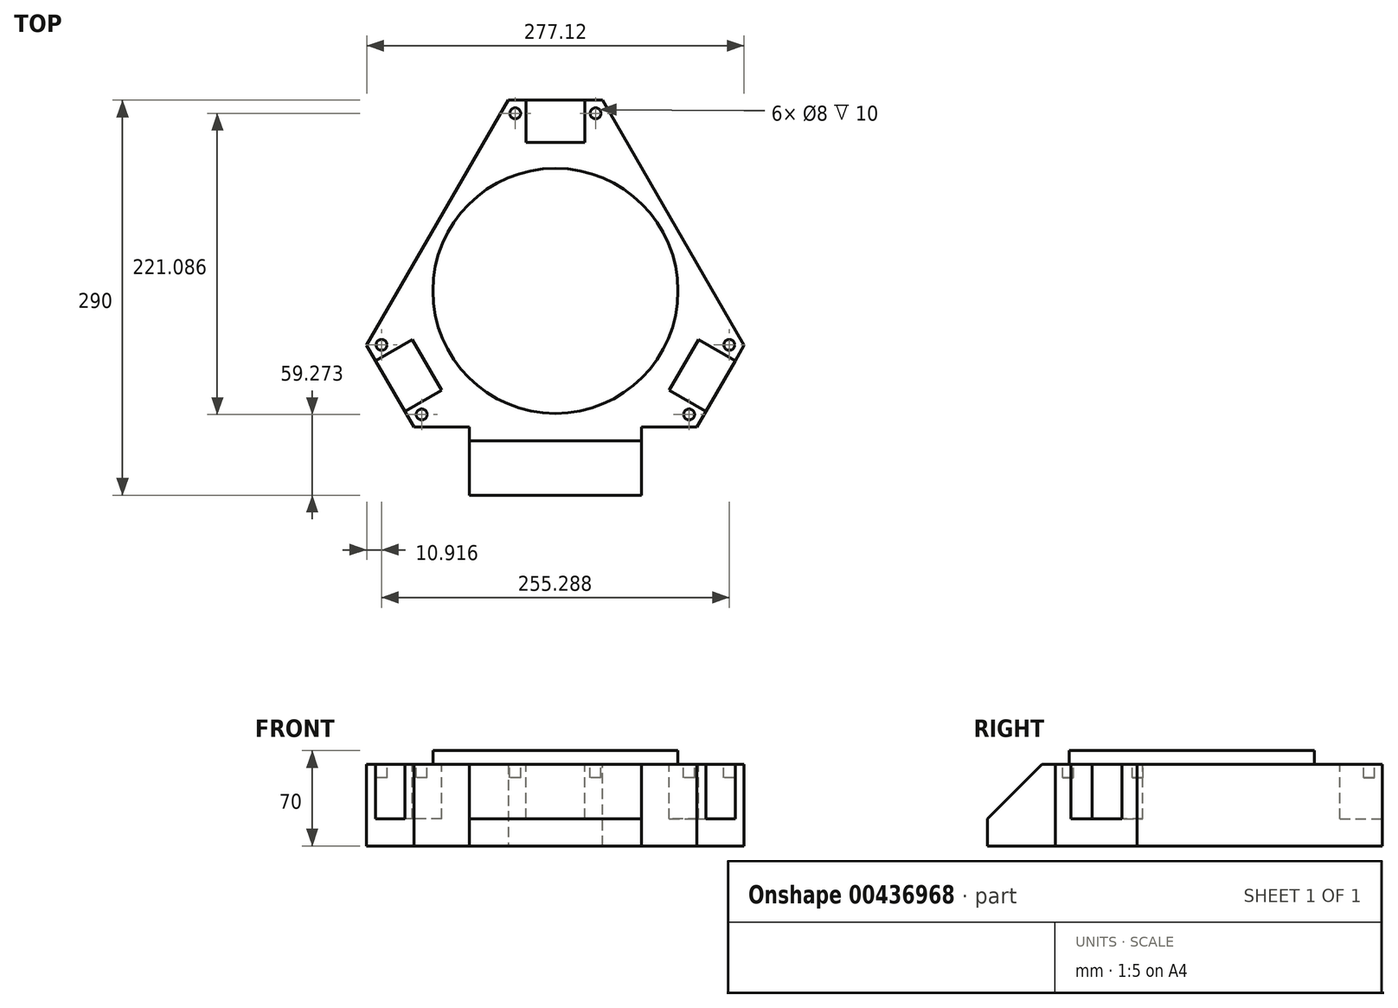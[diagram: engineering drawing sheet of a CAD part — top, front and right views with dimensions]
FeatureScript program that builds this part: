
annotation { "Feature Type Name" : "Feature", "Feature Type Description" : "" }
export const myFeature = defineFeature(function(context is Context, id is Id, definition is map)
    precondition{}
    {
        {
            var Q0;
            Q0=qCreatedBy(makeId("Top.planeOp"),FACE);
            var sketch = newSketch(context, id + "F0", { "sketchPlane" : qUnion([Q0])});
            skCircle(sketch, "E0.cCircle", {"center": v(0, 0) * mm, "radius": 100 * mm, "construction": true});
            skLineSegment(sketch, "E0.0", {"start": v(173.2, -100) * mm, "end": v(-173.2, -100) * mm});
            skLineSegment(sketch, "E0.1", {"start": v(-173.2, -100) * mm, "end": v(0, 200) * mm});
            skLineSegment(sketch, "E0.2", {"start": v(0, 200) * mm, "end": v(173.2, -100) * mm});
            skPoint(sketch, "E0.0.midPoint", {"position": v(0, -100) * mm});
            skSolve(sketch);
        }
        {
            var Q0;
            Q0=qSketchRegion(id+"F0",true);
            extrude(context, id + "F1", {"entities" : qUnion([Q0]), "depth" : 60 * mm});
        }
        {
            var Q0;
            Q0=makeQuery(id+"F1.opExtrude","SWEPT_EDGE",EDGE,{"disambiguationData":[OSD([sQuery(id+"F0.wireOp",EDGE,"E0.0"),sQuery(id+"F0.wireOp",EDGE,"E0.1")])]});
            var Q1;
            Q1=makeQuery(id+"F1.opExtrude","SWEPT_EDGE",EDGE,{"disambiguationData":[OSD([sQuery(id+"F0.wireOp",EDGE,"E0.0"),sQuery(id+"F0.wireOp",EDGE,"E0.2")])]});
            var Q2;
            Q2=makeQuery(id+"F1.opExtrude","SWEPT_EDGE",EDGE,{"disambiguationData":[OSD([sQuery(id+"F0.wireOp",EDGE,"E0.1"),sQuery(id+"F0.wireOp",EDGE,"E0.2")])]});
            chamfer(context, id + "F2", {"entities" : qUnion([Q0, Q1, Q2]), "width" : 40 * mm, "tangentPropagation" : true});
        }
        {
            var Q0;
            Q0=makeQuery(id+"F1.opExtrude","CAP_FACE",FACE,{"disambiguationData":[OSD([sQuery(id+"F0.wireOp",EDGE,"E0.0"),sQuery(id+"F0.wireOp",EDGE,"E0.1"),sQuery(id+"F0.wireOp",EDGE,"E0.2")])],"isStart":false});
            var sketch = newSketch(context, id + "F3", { "sketchPlane" : qUnion([Q0])});
            skCircle(sketch, "E1", {"center": v(0, 0) * mm, "radius": 90 * mm});
            skSolve(sketch);
        }
        {
            var Q0;
            Q0=qSketchRegion(id+"F3",true);
            extrude(context, id + "F4", {"entities" : qUnion([Q0]), "operationType" : NewBodyOperationType.ADD, "depth" : 10 * mm});
        }
        {
            var Q0;
            Q0=makeQuery(id+"F1.opExtrude","CAP_FACE",FACE,{"disambiguationData":[OSD([sQuery(id+"F0.wireOp",EDGE,"E0.0"),sQuery(id+"F0.wireOp",EDGE,"E0.1"),sQuery(id+"F0.wireOp",EDGE,"E0.2")])],"isStart":false});
            var sketch = newSketch(context, id + "F5", { "sketchPlane" : qUnion([Q0])});
            skLineSegment(sketch, "E2.bottom", {"start": v(-21.5, 108.86) * mm, "end": v(21.5, 108.86) * mm});
            skLineSegment(sketch, "E2.top", {"start": v(-21.5, 151.86) * mm, "end": v(21.5, 151.86) * mm});
            skLineSegment(sketch, "E2.left", {"start": v(-21.5, 108.86) * mm, "end": v(-21.5, 151.86) * mm});
            skLineSegment(sketch, "E2.right", {"start": v(21.5, 108.86) * mm, "end": v(21.5, 151.86) * mm});
            skPoint(sketch, "E2.middle", {"position": v(0, 130.36) * mm});
            skLineSegment(sketch, "E3.1.0", {"start": v(-83.52, -73.05) * mm, "end": v(-105.02, -35.8) * mm});
            skPoint(sketch, "E3.1.1", {"position": v(-112.9, -65.18) * mm});
            skLineSegment(sketch, "E3.1.2", {"start": v(-105.02, -35.8) * mm, "end": v(-142.26, -57.3) * mm});
            skLineSegment(sketch, "E3.1.3", {"start": v(-83.52, -73.05) * mm, "end": v(-120.76, -94.55) * mm});
            skLineSegment(sketch, "E3.1.4", {"start": v(-120.76, -94.55) * mm, "end": v(-142.26, -57.3) * mm});
            skLineSegment(sketch, "E3.2.0", {"start": v(105.02, -35.8) * mm, "end": v(83.52, -73.05) * mm});
            skPoint(sketch, "E3.2.1", {"position": v(112.9, -65.18) * mm});
            skLineSegment(sketch, "E3.2.2", {"start": v(83.52, -73.05) * mm, "end": v(120.76, -94.55) * mm});
            skLineSegment(sketch, "E3.2.3", {"start": v(105.02, -35.8) * mm, "end": v(142.26, -57.3) * mm});
            skLineSegment(sketch, "E3.2.4", {"start": v(142.26, -57.3) * mm, "end": v(120.76, -94.55) * mm});
            skPoint(sketch, "E3.center", {"position": v(0, 0) * mm});
            skSolve(sketch);
        }
        {
            var Q0;
            Q0=qSketchRegion(id+"F5",true);
            extrude(context, id + "F6", {"entities" : qUnion([Q0]), "operationType" : NewBodyOperationType.REMOVE, "oppositeDirection" : true, "depth" : 40 * mm});
        }
        {
            var Q0;
            Q0=makeQuery(id+"F1.opExtrude","CAP_FACE",FACE,{"disambiguationData":[OSD([sQuery(id+"F0.wireOp",EDGE,"E0.0"),sQuery(id+"F0.wireOp",EDGE,"E0.1"),sQuery(id+"F0.wireOp",EDGE,"E0.2")])],"isStart":false});
            var sketch = newSketch(context, id + "F7", { "sketchPlane" : qUnion([Q0])});
            skCircle(sketch, "E4", {"center": v(-29.5, 130.36) * mm, "radius": 4 * mm});
            skPoint(sketch, "E4.centerSnap0", {"position": v(-21.5, 130.36) * mm});
            skCircle(sketch, "E5", {"center": v(29.5, 130.36) * mm, "radius": 4 * mm});
            skPoint(sketch, "E5.centerSnap0", {"position": v(21.5, 130.36) * mm});
            skCircle(sketch, "E6.1.0", {"center": v(-98.14, -90.73) * mm, "radius": 4 * mm});
            skCircle(sketch, "E6.1.1", {"center": v(-127.64, -39.63) * mm, "radius": 4 * mm});
            skCircle(sketch, "E6.2.0", {"center": v(127.64, -39.63) * mm, "radius": 4 * mm});
            skCircle(sketch, "E6.2.1", {"center": v(98.14, -90.73) * mm, "radius": 4 * mm});
            skPoint(sketch, "E6.center", {"position": v(0, 0) * mm});
            skSolve(sketch);
        }
        {
            var Q0;
            Q0=qSketchRegion(id+"F7",true);
            extrude(context, id + "F8", {"entities" : qUnion([Q0]), "operationType" : NewBodyOperationType.REMOVE, "oppositeDirection" : true, "depth" : 10 * mm});
        }
        {
            var Q0;
            Q0=makeQuery(id+"F1.opExtrude","SWEPT_FACE",FACE,{"disambiguationData":[OSD([sQuery(id+"F0.wireOp",EDGE,"E0.0")])]});
            var sketch = newSketch(context, id + "F9", { "sketchPlane" : qUnion([Q0])});
            skLineSegment(sketch, "E7.bottom", {"start": v(-63.2, 60) * mm, "end": v(63.2, 60) * mm});
            skLineSegment(sketch, "E7.top", {"start": v(-63.2, 0) * mm, "end": v(63.2, 0) * mm});
            skLineSegment(sketch, "E7.left", {"start": v(-63.2, 60) * mm, "end": v(-63.2, 0) * mm});
            skLineSegment(sketch, "E7.right", {"start": v(63.2, 60) * mm, "end": v(63.2, 0) * mm});
            skSolve(sketch);
        }
        {
            var Q0;
            Q0=makeQuery(id+"F9.imprint","IMPRINT",FACE,{"disambiguationData":[TD([[makeQuery(id+"F9.imprint","IMPRINT",EDGE,{"derivedFrom":sQuery(id+"F9.wireOp",EDGE,"E7.bottom")}),1.0]])]});
            extrude(context, id + "F10", {"entities" : qUnion([Q0]), "operationType" : NewBodyOperationType.ADD, "depth" : 50 * mm});
        }
        {
            var Q0;
            Q0=makeQuery(id+"F10.opExtrude","CAP_EDGE",EDGE,{"disambiguationData":[OSD([sQuery(id+"F9.wireOp",EDGE,"E7.bottom")])],"isStart":false});
            chamfer(context, id + "F11", {"entities" : qUnion([Q0]), "width" : 40 * mm, "tangentPropagation" : true});
        }
    });
